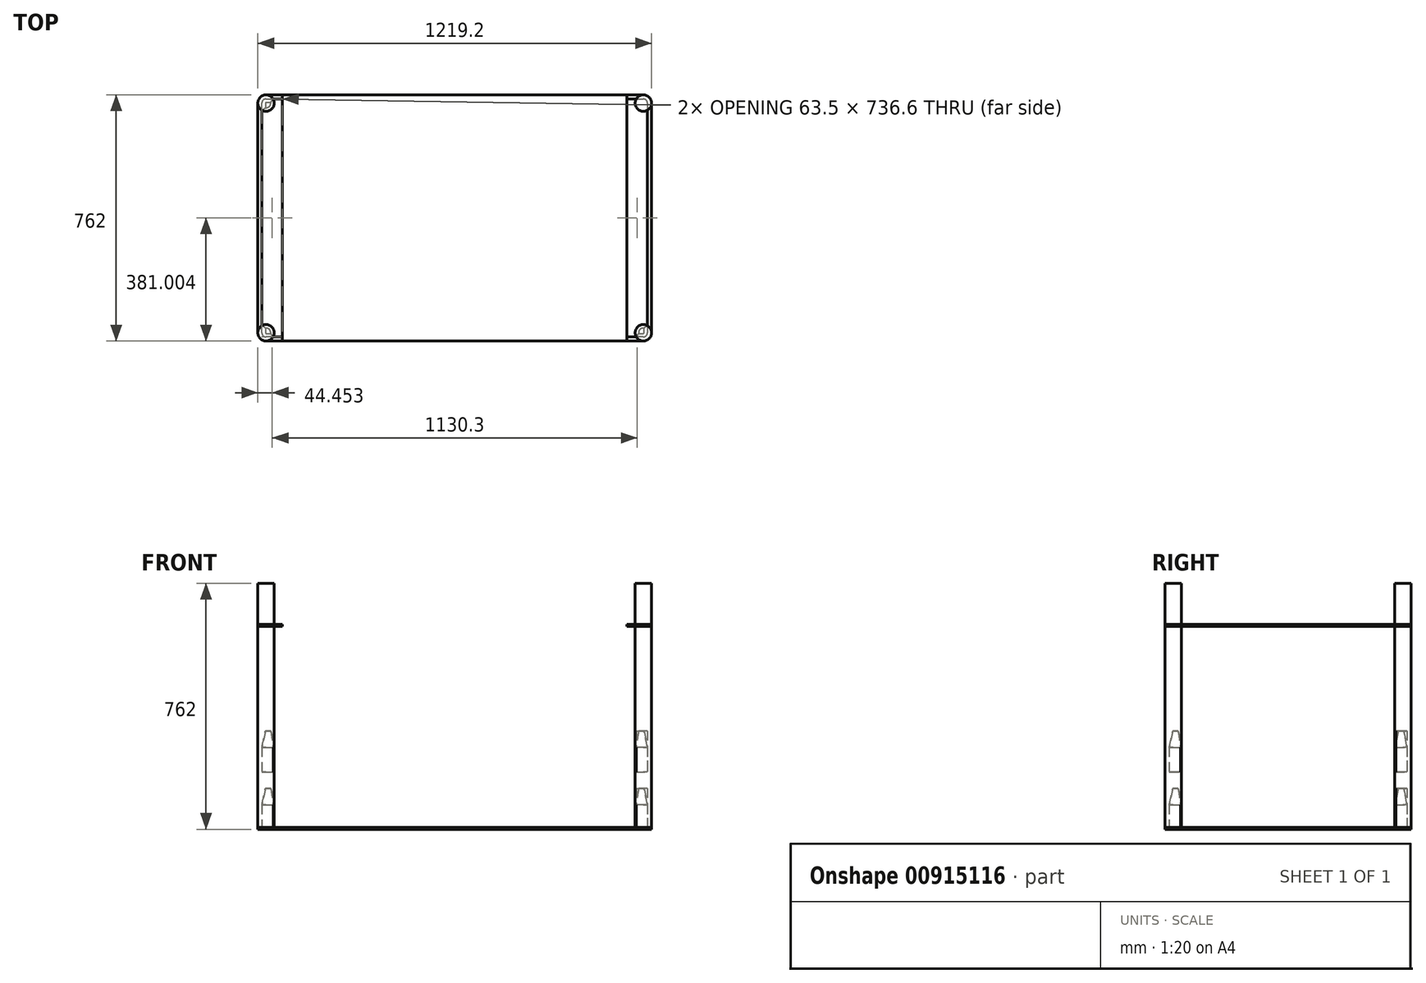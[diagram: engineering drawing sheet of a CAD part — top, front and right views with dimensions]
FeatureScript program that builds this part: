
annotation { "Feature Type Name" : "Feature", "Feature Type Description" : "" }
export const myFeature = defineFeature(function(context is Context, id is Id, definition is map)
    precondition{}
    {
        {
            var Q0;
            Q0=qCreatedBy(makeId("Top.planeOp"),FACE);
            var sketch = newSketch(context, id + "F0", { "sketchPlane" : qUnion([Q0])});
            skLineSegment(sketch, "E0.bottom", {"start": v(-586.7, 384.86) * mm, "end": v(581.7, 384.86) * mm});
            skLineSegment(sketch, "E0.top", {"start": v(-586.7, -377.14) * mm, "end": v(581.7, -377.14) * mm});
            skLineSegment(sketch, "E0.left", {"start": v(-612.1, 359.46) * mm, "end": v(-612.1, -351.74) * mm});
            skLineSegment(sketch, "E0.right", {"start": v(607.1, 359.46) * mm, "end": v(607.1, -351.74) * mm});
            skLineSegment(sketch, "E1", {"start": v(-535.9, 384.86) * mm, "end": v(-535.9, -377.14) * mm});
            skLineSegment(sketch, "E2", {"start": v(530.9, 384.86) * mm, "end": v(530.9, -377.14) * mm});
            skPoint(sketch, "E3.visualSharp", {"position": v(-612.1, 384.86) * mm});
            skArc(sketch, "E3.filletArc", {"start": v(-586.7, 384.86) * mm, "mid": v(-604.67, 377.42) * mm, "end": v(-612.1, 359.46) * mm});
            skPoint(sketch, "E4.visualSharp", {"position": v(-612.1, -377.14) * mm});
            skArc(sketch, "E4.filletArc", {"start": v(-612.1, -351.74) * mm, "mid": v(-604.67, -369.7) * mm, "end": v(-586.7, -377.14) * mm});
            skPoint(sketch, "E5.visualSharp", {"position": v(607.1, 384.86) * mm});
            skArc(sketch, "E5.filletArc", {"start": v(607.1, 359.46) * mm, "mid": v(599.65, 377.42) * mm, "end": v(581.7, 384.86) * mm});
            skPoint(sketch, "E6.visualSharp", {"position": v(607.1, -377.14) * mm});
            skArc(sketch, "E6.filletArc", {"start": v(581.7, -377.14) * mm, "mid": v(599.65, -369.7) * mm, "end": v(607.1, -351.74) * mm});
            skArc(sketch, "E7.0", {"start": v(-586.7, 372.16) * mm, "mid": v(-595.69, 368.44) * mm, "end": v(-599.4, 359.46) * mm});
            skLineSegment(sketch, "E7.1", {"start": v(-586.7, 372.16) * mm, "end": v(581.7, 372.16) * mm});
            skLineSegment(sketch, "E7.2", {"start": v(-599.4, 359.46) * mm, "end": v(-599.4, -351.74) * mm});
            skArc(sketch, "E7.3", {"start": v(594.4, 359.46) * mm, "mid": v(590.67, 368.44) * mm, "end": v(581.7, 372.16) * mm});
            skArc(sketch, "E7.4", {"start": v(-599.4, -351.74) * mm, "mid": v(-595.69, -360.72) * mm, "end": v(-586.7, -364.44) * mm});
            skLineSegment(sketch, "E7.5", {"start": v(-586.7, -364.44) * mm, "end": v(581.7, -364.44) * mm});
            skArc(sketch, "E7.6", {"start": v(581.7, -364.44) * mm, "mid": v(590.67, -360.72) * mm, "end": v(594.4, -351.74) * mm});
            skLineSegment(sketch, "E7.7", {"start": v(594.4, 359.46) * mm, "end": v(594.4, -351.74) * mm});
            skLineSegment(sketch, "E8.right", {"start": v(530.9, 237.71) * mm, "end": v(530.9, -219.49) * mm});
            skLineSegment(sketch, "E9.left", {"start": v(-599.4, 22.91) * mm, "end": v(-599.4, -15.19) * mm});
            skLineSegment(sketch, "E9.right", {"start": v(594.4, 22.91) * mm, "end": v(594.4, -15.19) * mm});
            skLineSegment(sketch, "E10.bottom", {"start": v(-421.6, 372.16) * mm, "end": v(-383.5, 372.16) * mm});
            skLineSegment(sketch, "E10.top", {"start": v(-421.6, -364.44) * mm, "end": v(-383.5, -364.44) * mm});
            skLineSegment(sketch, "E11.bottom", {"start": v(378.5, 372.16) * mm, "end": v(416.6, 372.16) * mm});
            skLineSegment(sketch, "E11.top", {"start": v(378.5, -364.44) * mm, "end": v(416.6, -364.44) * mm});
            skCircle(sketch, "E12", {"center": v(581.7, -351.74) * mm, "radius": 25.4 * mm});
            skCircle(sketch, "E13", {"center": v(581.7, 359.46) * mm, "radius": 25.4 * mm});
            skCircle(sketch, "E14", {"center": v(-586.7, 359.46) * mm, "radius": 25.4 * mm});
            skCircle(sketch, "E15", {"center": v(-586.7, -351.74) * mm, "radius": 25.4 * mm});
            skSolve(sketch);
        }
        {
            var Q0;
            {var subQ0=sQuery(id+"F0.wireOp",EDGE,"RHyDtdP4-Gck5-t29Y-2Plq-2zW18biPkiO3");Q0=makeQuery(id+"F0.imprint","IMPRINT",FACE,{"disambiguationData":[TD([[makeQuery(id+"F0.imprint","IMPRINT",EDGE,{"derivedFrom":subQ0}),1.0]])]});}
            var Q1;
            {var subQ0=sQuery(id+"F0.wireOp",EDGE,"YXO1ubsz-QMrO-05iV-85zx-2RvqL2AsMvx7");Q1=makeQuery(id+"F0.imprint","IMPRINT",FACE,{"disambiguationData":[TD([[makeQuery(id+"F0.imprint","IMPRINT",EDGE,{"derivedFrom":subQ0}),-1.0]])]});}
            var Q2;
            {var subQ0=sQuery(id+"F0.wireOp",EDGE,"1EET5IaC-rPqa-f1PM-2F6D-7rHTKaeenNsA");Q2=makeQuery(id+"F0.imprint","IMPRINT",FACE,{"disambiguationData":[TD([[makeQuery(id+"F0.imprint","IMPRINT",EDGE,{"derivedFrom":subQ0}),-1.0]])]});}
            var Q3;
            {var subQ0=sQuery(id+"F0.wireOp",EDGE,"E8.right");Q3=makeQuery(id+"F0.imprint","IMPRINT",FACE,{"disambiguationData":[TD([[makeQuery(id+"F0.imprint","IMPRINT",EDGE,{"derivedFrom":subQ0}),-1.0]])]});}
            var Q4;
            {var subQ0=sQuery(id+"F0.wireOp",EDGE,"E1");var subQ1=sQuery(id+"F0.wireOp",EDGE,"E0.bottom");var subQ2=makeQuery(id+"F0.imprint","INTERSECT",VERTEX,{"derivedFrom":[subQ1,subQ0]});Q4=makeQuery(id+"F0.imprint","IMPRINT",FACE,{"disambiguationData":[TD([[makeQuery(id+"F0.imprint","IMPRINT",EDGE,{"disambiguationData":[TD([[subQ2,-1.0]])],"derivedFrom":subQ1}),-1.0]])]});}
            var Q5;
            {var subQ0=sQuery(id+"F0.wireOp",EDGE,"E1");var subQ1=sQuery(id+"F0.wireOp",EDGE,"E0.top");var subQ2=makeQuery(id+"F0.imprint","INTERSECT",VERTEX,{"derivedFrom":[subQ1,subQ0]});Q5=makeQuery(id+"F0.imprint","IMPRINT",FACE,{"disambiguationData":[TD([[makeQuery(id+"F0.imprint","IMPRINT",EDGE,{"disambiguationData":[TD([[subQ2,-1.0]])],"derivedFrom":subQ1}),1.0]])]});}
            var Q6;
            Q6=makeQuery(id+"F0.imprint","IMPRINT",FACE,{"disambiguationData":[TD([[makeQuery(id+"F0.imprint","IMPRINT",EDGE,{"derivedFrom":sQuery(id+"F0.wireOp",EDGE,"E0.right")}),-1.0]])]});
            var Q7;
            Q7=makeQuery(id+"F0.imprint","IMPRINT",FACE,{"disambiguationData":[TD([[makeQuery(id+"F0.imprint","IMPRINT",EDGE,{"derivedFrom":sQuery(id+"F0.wireOp",EDGE,"E0.left")}),1.0]])]});
            var Q8;
            {var subQ1=sQuery(id+"F0.wireOp",EDGE,"E7.0");Q8=makeQuery(id+"F0.imprint","IMPRINT",FACE,{"disambiguationData":[TD([[makeQuery(id+"F0.imprint","IMPRINT",EDGE,{"derivedFrom":subQ1}),1.0]])]});}
            var Q9;
            {var subQ0=sQuery(id+"F0.wireOp",EDGE,"E7.3");Q9=makeQuery(id+"F0.imprint","IMPRINT",FACE,{"disambiguationData":[TD([[makeQuery(id+"F0.imprint","IMPRINT",EDGE,{"derivedFrom":subQ0}),1.0]])]});}
            var Q10;
            {var subQ1=sQuery(id+"F0.wireOp",EDGE,"E1");var subQ4=sQuery(id+"F0.wireOp",EDGE,"E7.1");var subQ5=makeQuery(id+"F0.imprint","INTERSECT",VERTEX,{"derivedFrom":[subQ1,subQ4]});Q10=makeQuery(id+"F0.imprint","IMPRINT",FACE,{"disambiguationData":[TD([[makeQuery(id+"F0.imprint","IMPRINT",EDGE,{"disambiguationData":[TD([[subQ5,-1.0]])],"derivedFrom":subQ4}),-1.0]])]});}
            var Q11;
            {var subQ1=sQuery(id+"F0.wireOp",EDGE,"E1");var subQ4=sQuery(id+"F0.wireOp",EDGE,"E7.5");var subQ5=makeQuery(id+"F0.imprint","INTERSECT",VERTEX,{"derivedFrom":[subQ1,subQ4]});Q11=makeQuery(id+"F0.imprint","IMPRINT",FACE,{"disambiguationData":[TD([[makeQuery(id+"F0.imprint","IMPRINT",EDGE,{"disambiguationData":[TD([[subQ5,-1.0]])],"derivedFrom":subQ4}),1.0]])]});}
            var Q12;
            {var subQ0=sQuery(id+"F0.wireOp",EDGE,"E8.left");Q12=makeQuery(id+"F0.imprint","IMPRINT",FACE,{"disambiguationData":[TD([[makeQuery(id+"F0.imprint","IMPRINT",EDGE,{"derivedFrom":subQ0}),1.0]])]});}
            var Q13;
            {var subQ0=sQuery(id+"F0.wireOp",EDGE,"E7.4");Q13=makeQuery(id+"F0.imprint","IMPRINT",FACE,{"disambiguationData":[TD([[makeQuery(id+"F0.imprint","IMPRINT",EDGE,{"derivedFrom":subQ0}),1.0]])]});}
            var Q14;
            {var subQ5=sQuery(id+"F0.wireOp",EDGE,"E9.left");Q14=makeQuery(id+"F0.imprint","IMPRINT",FACE,{"disambiguationData":[TD([[makeQuery(id+"F0.imprint","IMPRINT",EDGE,{"derivedFrom":subQ5}),1.0]])]});}
            var Q15;
            {var subQ0=sQuery(id+"F0.wireOp",EDGE,"E9.bottom");var subQ1=sQuery(id+"F0.wireOp",EDGE,"E1");var subQ2=makeQuery(id+"F0.imprint","INTERSECT",VERTEX,{"derivedFrom":[subQ1,subQ0]});Q15=makeQuery(id+"F0.imprint","IMPRINT",FACE,{"disambiguationData":[TD([[makeQuery(id+"F0.imprint","IMPRINT",EDGE,{"disambiguationData":[TD([[subQ2,-1.0]])],"derivedFrom":subQ1}),1.0]])]});}
            var Q16;
            {var subQ0=sQuery(id+"F0.wireOp",EDGE,"E10.right");var subQ5=sQuery(id+"F0.wireOp",EDGE,"E9.top");var subQ6=makeQuery(id+"F0.imprint","INTERSECT",VERTEX,{"derivedFrom":[subQ5,subQ0]});Q16=makeQuery(id+"F0.imprint","IMPRINT",FACE,{"disambiguationData":[TD([[makeQuery(id+"F0.imprint","IMPRINT",EDGE,{"disambiguationData":[TD([[subQ6,-1.0]])],"derivedFrom":subQ5}),-1.0]])]});}
            var Q17;
            {var subQ0=sQuery(id+"F0.wireOp",EDGE,"E10.right");var subQ5=sQuery(id+"F0.wireOp",EDGE,"E9.bottom");var subQ6=makeQuery(id+"F0.imprint","INTERSECT",VERTEX,{"derivedFrom":[subQ5,subQ0]});Q17=makeQuery(id+"F0.imprint","IMPRINT",FACE,{"disambiguationData":[TD([[makeQuery(id+"F0.imprint","IMPRINT",EDGE,{"disambiguationData":[TD([[subQ6,-1.0]])],"derivedFrom":subQ5}),1.0]])]});}
            var Q18;
            {var subQ5=sQuery(id+"F0.wireOp",EDGE,"E10.bottom");Q18=makeQuery(id+"F0.imprint","IMPRINT",FACE,{"disambiguationData":[TD([[makeQuery(id+"F0.imprint","IMPRINT",EDGE,{"derivedFrom":subQ5}),-1.0]])]});}
            var Q19;
            {var subQ0=sQuery(id+"F0.wireOp",EDGE,"E10.left");var subQ1=sQuery(id+"F0.wireOp",EDGE,"E9.bottom");var subQ2=makeQuery(id+"F0.imprint","INTERSECT",VERTEX,{"derivedFrom":[subQ1,subQ0]});Q19=makeQuery(id+"F0.imprint","IMPRINT",FACE,{"disambiguationData":[TD([[makeQuery(id+"F0.imprint","IMPRINT",EDGE,{"disambiguationData":[TD([[subQ2,-1.0]])],"derivedFrom":subQ1}),-1.0]])]});}
            var Q20;
            {var subQ5=sQuery(id+"F0.wireOp",EDGE,"E10.top");Q20=makeQuery(id+"F0.imprint","IMPRINT",FACE,{"disambiguationData":[TD([[makeQuery(id+"F0.imprint","IMPRINT",EDGE,{"derivedFrom":subQ5}),1.0]])]});}
            var Q21;
            {var subQ0=sQuery(id+"F0.wireOp",EDGE,"E10.right");var subQ1=sQuery(id+"F0.wireOp",EDGE,"E9.bottom");var subQ2=makeQuery(id+"F0.imprint","INTERSECT",VERTEX,{"derivedFrom":[subQ1,subQ0]});Q21=makeQuery(id+"F0.imprint","IMPRINT",FACE,{"disambiguationData":[TD([[makeQuery(id+"F0.imprint","IMPRINT",EDGE,{"disambiguationData":[TD([[subQ2,-1.0]])],"derivedFrom":subQ1}),-1.0]])]});}
            var Q22;
            {var subQ0=sQuery(id+"F0.wireOp",EDGE,"E8.right");var subQ1=sQuery(id+"F0.wireOp",EDGE,"E2");var subQ2=makeQuery(id+"F0.imprint","INTERSECT",VERTEX,{"disambiguationData":[OD(1.0)],"derivedFrom":[subQ1,subQ0]});Q22=makeQuery(id+"F0.imprint","IMPRINT",FACE,{"disambiguationData":[TD([[makeQuery(id+"F0.imprint","IMPRINT",EDGE,{"disambiguationData":[TD([[subQ2,-1.0]])],"derivedFrom":subQ1}),-1.0]])]});}
            var Q23;
            {var subQ1=sQuery(id+"F0.wireOp",EDGE,"E8.right");var subQ7=sQuery(id+"F0.wireOp",EDGE,"E2");var subQ9=makeQuery(id+"F0.imprint","INTERSECT",VERTEX,{"disambiguationData":[OD(0.0)],"derivedFrom":[subQ7,subQ1]});Q23=makeQuery(id+"F0.imprint","IMPRINT",FACE,{"disambiguationData":[TD([[makeQuery(id+"F0.imprint","IMPRINT",EDGE,{"disambiguationData":[TD([[subQ9,1.0]])],"derivedFrom":subQ7}),-1.0]])]});}
            var Q24;
            {var subQ5=sQuery(id+"F0.wireOp",EDGE,"E11.bottom");Q24=makeQuery(id+"F0.imprint","IMPRINT",FACE,{"disambiguationData":[TD([[makeQuery(id+"F0.imprint","IMPRINT",EDGE,{"derivedFrom":subQ5}),-1.0]])]});}
            var Q25;
            {var subQ0=sQuery(id+"F0.wireOp",EDGE,"E11.left");var subQ1=sQuery(id+"F0.wireOp",EDGE,"E9.bottom");var subQ2=makeQuery(id+"F0.imprint","INTERSECT",VERTEX,{"derivedFrom":[subQ1,subQ0]});Q25=makeQuery(id+"F0.imprint","IMPRINT",FACE,{"disambiguationData":[TD([[makeQuery(id+"F0.imprint","IMPRINT",EDGE,{"disambiguationData":[TD([[subQ2,-1.0]])],"derivedFrom":subQ1}),-1.0]])]});}
            var Q26;
            {var subQ5=sQuery(id+"F0.wireOp",EDGE,"E11.top");Q26=makeQuery(id+"F0.imprint","IMPRINT",FACE,{"disambiguationData":[TD([[makeQuery(id+"F0.imprint","IMPRINT",EDGE,{"derivedFrom":subQ5}),1.0]])]});}
            var Q27;
            {var subQ1=sQuery(id+"F0.wireOp",EDGE,"E7.6");Q27=makeQuery(id+"F0.imprint","IMPRINT",FACE,{"disambiguationData":[TD([[makeQuery(id+"F0.imprint","IMPRINT",EDGE,{"derivedFrom":subQ1}),1.0]])]});}
            var Q28;
            {var subQ5=sQuery(id+"F0.wireOp",EDGE,"E9.right");Q28=makeQuery(id+"F0.imprint","IMPRINT",FACE,{"disambiguationData":[TD([[makeQuery(id+"F0.imprint","IMPRINT",EDGE,{"derivedFrom":subQ5}),-1.0]])]});}
            var Q29;
            {var subQ4=sQuery(id+"F0.wireOp",EDGE,"E7.6");Q29=makeQuery(id+"F0.imprint","IMPRINT",FACE,{"disambiguationData":[TD([[makeQuery(id+"F0.imprint","IMPRINT",EDGE,{"derivedFrom":subQ4}),-1.0]])]});}
            var Q30;
            {var subQ0=sQuery(id+"F0.wireOp",EDGE,"E12");var subQ1=sQuery(id+"F0.wireOp",EDGE,"E0.top");var subQ2=makeQuery(id+"F0.imprint","INTERSECT",VERTEX,{"derivedFrom":[subQ1,subQ0]});Q30=makeQuery(id+"F0.imprint","IMPRINT",FACE,{"disambiguationData":[TD([[makeQuery(id+"F0.imprint","IMPRINT",EDGE,{"disambiguationData":[TD([[subQ2,1.0]])],"derivedFrom":subQ1}),1.0]])]});}
            var Q31;
            {var subQ4=sQuery(id+"F0.wireOp",EDGE,"E7.3");Q31=makeQuery(id+"F0.imprint","IMPRINT",FACE,{"disambiguationData":[TD([[makeQuery(id+"F0.imprint","IMPRINT",EDGE,{"derivedFrom":subQ4}),-1.0]])]});}
            var Q32;
            {var subQ0=sQuery(id+"F0.wireOp",EDGE,"E13");var subQ1=sQuery(id+"F0.wireOp",EDGE,"E0.bottom");var subQ2=makeQuery(id+"F0.imprint","INTERSECT",VERTEX,{"derivedFrom":[subQ1,subQ0]});Q32=makeQuery(id+"F0.imprint","IMPRINT",FACE,{"disambiguationData":[TD([[makeQuery(id+"F0.imprint","IMPRINT",EDGE,{"disambiguationData":[TD([[subQ2,1.0]])],"derivedFrom":subQ1}),-1.0]])]});}
            var Q33;
            {var subQ0=sQuery(id+"F0.wireOp",EDGE,"E15");var subQ1=sQuery(id+"F0.wireOp",EDGE,"E0.top");var subQ2=makeQuery(id+"F0.imprint","INTERSECT",VERTEX,{"derivedFrom":[subQ1,subQ0]});Q33=makeQuery(id+"F0.imprint","IMPRINT",FACE,{"disambiguationData":[TD([[makeQuery(id+"F0.imprint","IMPRINT",EDGE,{"disambiguationData":[TD([[subQ2,-1.0]])],"derivedFrom":subQ1}),1.0]])]});}
            var Q34;
            {var subQ5=sQuery(id+"F0.wireOp",EDGE,"E7.4");Q34=makeQuery(id+"F0.imprint","IMPRINT",FACE,{"disambiguationData":[TD([[makeQuery(id+"F0.imprint","IMPRINT",EDGE,{"derivedFrom":subQ5}),-1.0]])]});}
            var Q35;
            {var subQ0=sQuery(id+"F0.wireOp",EDGE,"E14");var subQ1=sQuery(id+"F0.wireOp",EDGE,"E0.bottom");var subQ2=makeQuery(id+"F0.imprint","INTERSECT",VERTEX,{"derivedFrom":[subQ1,subQ0]});Q35=makeQuery(id+"F0.imprint","IMPRINT",FACE,{"disambiguationData":[TD([[makeQuery(id+"F0.imprint","IMPRINT",EDGE,{"disambiguationData":[TD([[subQ2,-1.0]])],"derivedFrom":subQ1}),-1.0]])]});}
            var Q36;
            {var subQ1=sQuery(id+"F0.wireOp",EDGE,"E7.0");Q36=makeQuery(id+"F0.imprint","IMPRINT",FACE,{"disambiguationData":[TD([[makeQuery(id+"F0.imprint","IMPRINT",EDGE,{"derivedFrom":subQ1}),-1.0]])]});}
            extrude(context, id + "F1", {"entities" : qUnion([Q0, Q1, Q2, Q3, Q4, Q5, Q6, Q7, Q8, Q9, Q10, Q11, Q12, Q13, Q14, Q15, Q16, Q17, Q18, Q19, Q20, Q21, Q22, Q23, Q24, Q25, Q26, Q27, Q28, Q29, Q30, Q31, Q32, Q33, Q34, Q35, Q36]), "depth" : 6.35 * mm, "offsetDistance" : 25.4 * mm});
        }
        {
            var Q0;
            {var subQ9=sQuery(id+"F0.wireOp",EDGE,"E8.right");Q0=makeQuery(id+"F0.imprint","IMPRINT",FACE,{"disambiguationData":[TD([[makeQuery(id+"F0.imprint","IMPRINT",EDGE,{"derivedFrom":subQ9}),-1.0]])]});}
            var Q1;
            {var subQ0=sQuery(id+"F0.wireOp",EDGE,"E9.left");Q1=makeQuery(id+"F0.imprint","IMPRINT",FACE,{"disambiguationData":[TD([[makeQuery(id+"F0.imprint","IMPRINT",EDGE,{"derivedFrom":subQ0}),1.0]])]});}
            var Q2;
            {var subQ5=sQuery(id+"F0.wireOp",EDGE,"E8.right");Q2=makeQuery(id+"F0.imprint","IMPRINT",FACE,{"disambiguationData":[TD([[makeQuery(id+"F0.imprint","IMPRINT",EDGE,{"derivedFrom":subQ5}),1.0]])]});}
            var Q3;
            {var subQ0=sQuery(id+"F0.wireOp",EDGE,"E7.0");Q3=makeQuery(id+"F0.imprint","IMPRINT",FACE,{"disambiguationData":[TD([[makeQuery(id+"F0.imprint","IMPRINT",EDGE,{"derivedFrom":subQ0}),1.0]])]});}
            var Q4;
            {var subQ0=sQuery(id+"F0.wireOp",EDGE,"E7.3");Q4=makeQuery(id+"F0.imprint","IMPRINT",FACE,{"disambiguationData":[TD([[makeQuery(id+"F0.imprint","IMPRINT",EDGE,{"derivedFrom":subQ0}),1.0]])]});}
            var Q5;
            {var subQ0=sQuery(id+"F0.wireOp",EDGE,"E7.4");Q5=makeQuery(id+"F0.imprint","IMPRINT",FACE,{"disambiguationData":[TD([[makeQuery(id+"F0.imprint","IMPRINT",EDGE,{"derivedFrom":subQ0}),1.0]])]});}
            var Q6;
            {var subQ0=sQuery(id+"F0.wireOp",EDGE,"E7.6");Q6=makeQuery(id+"F0.imprint","IMPRINT",FACE,{"disambiguationData":[TD([[makeQuery(id+"F0.imprint","IMPRINT",EDGE,{"derivedFrom":subQ0}),1.0]])]});}
            extrude(context, id + "F2", {"entities" : qUnion([Q0, Q1, Q2, Q3, Q4, Q5, Q6]), "depth" : 127 * mm, "offsetDistance" : 25.4 * mm, "hasSecondDirection" : true, "secondDirectionOppositeDirection" : false, "secondDirectionDepth" : 6.35 * mm});
        }
        {
            var Q0;
            Q0=makeQuery(id+"F2.opExtrude","CAP_FACE",FACE,{"disambiguationData":[OSD([sQuery(id+"F0.wireOp",EDGE,"E7.0"),sQuery(id+"F0.wireOp",EDGE,"E7.1"),sQuery(id+"F0.wireOp",EDGE,"E7.2"),sQuery(id+"F0.wireOp",EDGE,"E7.3"),sQuery(id+"F0.wireOp",EDGE,"E7.4"),sQuery(id+"F0.wireOp",EDGE,"E7.5"),sQuery(id+"F0.wireOp",EDGE,"E7.6"),sQuery(id+"F0.wireOp",EDGE,"E7.7"),sQuery(id+"F0.wireOp",EDGE,"E9.left"),sQuery(id+"F0.wireOp",EDGE,"E9.right"),sQuery(id+"F0.wireOp",EDGE,"E10.bottom"),sQuery(id+"F0.wireOp",EDGE,"E10.top"),sQuery(id+"F0.wireOp",EDGE,"E11.bottom"),sQuery(id+"F0.wireOp",EDGE,"E11.top")])],"isStart":false});
            chamfer(context, id + "F3", {"entities" : qUnion([Q0]), "chamferType" : ChamferType.OFFSET_ANGLE, "width" : 50.8 * mm, "oppositeDirection" : true, "angle" : 12 * degree, "tangentPropagation" : true});
        }
        {
            var Q0;
            {var subQ4=sQuery(id+"F0.wireOp",EDGE,"E7.6");Q0=makeQuery(id+"F0.imprint","IMPRINT",FACE,{"disambiguationData":[TD([[makeQuery(id+"F0.imprint","IMPRINT",EDGE,{"derivedFrom":subQ4}),-1.0]])]});}
            var Q1;
            {var subQ0=sQuery(id+"F0.wireOp",EDGE,"E7.6");Q1=makeQuery(id+"F0.imprint","IMPRINT",FACE,{"disambiguationData":[TD([[makeQuery(id+"F0.imprint","IMPRINT",EDGE,{"derivedFrom":subQ0}),1.0]])]});}
            var Q2;
            {var subQ0=sQuery(id+"F0.wireOp",EDGE,"E7.0");Q2=makeQuery(id+"F0.imprint","IMPRINT",FACE,{"disambiguationData":[TD([[makeQuery(id+"F0.imprint","IMPRINT",EDGE,{"derivedFrom":subQ0}),1.0]])]});}
            var Q3;
            {var subQ1=sQuery(id+"F0.wireOp",EDGE,"E7.0");Q3=makeQuery(id+"F0.imprint","IMPRINT",FACE,{"disambiguationData":[TD([[makeQuery(id+"F0.imprint","IMPRINT",EDGE,{"derivedFrom":subQ1}),-1.0]])]});}
            var Q4;
            {var subQ0=sQuery(id+"F0.wireOp",EDGE,"E7.4");Q4=makeQuery(id+"F0.imprint","IMPRINT",FACE,{"disambiguationData":[TD([[makeQuery(id+"F0.imprint","IMPRINT",EDGE,{"derivedFrom":subQ0}),1.0]])]});}
            var Q5;
            {var subQ5=sQuery(id+"F0.wireOp",EDGE,"E7.4");Q5=makeQuery(id+"F0.imprint","IMPRINT",FACE,{"disambiguationData":[TD([[makeQuery(id+"F0.imprint","IMPRINT",EDGE,{"derivedFrom":subQ5}),-1.0]])]});}
            var Q6;
            {var subQ4=sQuery(id+"F0.wireOp",EDGE,"E7.3");Q6=makeQuery(id+"F0.imprint","IMPRINT",FACE,{"disambiguationData":[TD([[makeQuery(id+"F0.imprint","IMPRINT",EDGE,{"derivedFrom":subQ4}),-1.0]])]});}
            var Q7;
            {var subQ0=sQuery(id+"F0.wireOp",EDGE,"E7.3");Q7=makeQuery(id+"F0.imprint","IMPRINT",FACE,{"disambiguationData":[TD([[makeQuery(id+"F0.imprint","IMPRINT",EDGE,{"derivedFrom":subQ0}),1.0]])]});}
            extrude(context, id + "F4", {"entities" : qUnion([Q0, Q1, Q2, Q3, Q4, Q5, Q6, Q7]), "depth" : 762 * mm, "offsetDistance" : 25.4 * mm, "hasSecondDirection" : true, "secondDirectionOppositeDirection" : false, "secondDirectionDepth" : 6.35 * mm});
        }
        {
            var Q0;
            {var subQ5=sQuery(id+"F0.wireOp",EDGE,"E0.left");Q0=makeQuery(id+"F0.imprint","IMPRINT",FACE,{"disambiguationData":[TD([[makeQuery(id+"F0.imprint","IMPRINT",EDGE,{"derivedFrom":subQ5}),1.0]])]});}
            var Q1;
            {var subQ0=sQuery(id+"F0.wireOp",EDGE,"E9.left");Q1=makeQuery(id+"F0.imprint","IMPRINT",FACE,{"disambiguationData":[TD([[makeQuery(id+"F0.imprint","IMPRINT",EDGE,{"derivedFrom":subQ0}),1.0]])]});}
            var Q2;
            {var subQ0=sQuery(id+"F0.wireOp",EDGE,"E7.0");Q2=makeQuery(id+"F0.imprint","IMPRINT",FACE,{"disambiguationData":[TD([[makeQuery(id+"F0.imprint","IMPRINT",EDGE,{"derivedFrom":subQ0}),1.0]])]});}
            var Q3;
            {var subQ1=sQuery(id+"F0.wireOp",EDGE,"E7.0");Q3=makeQuery(id+"F0.imprint","IMPRINT",FACE,{"disambiguationData":[TD([[makeQuery(id+"F0.imprint","IMPRINT",EDGE,{"derivedFrom":subQ1}),-1.0]])]});}
            var Q4;
            {var subQ9=sQuery(id+"F0.wireOp",EDGE,"E8.right");Q4=makeQuery(id+"F0.imprint","IMPRINT",FACE,{"disambiguationData":[TD([[makeQuery(id+"F0.imprint","IMPRINT",EDGE,{"derivedFrom":subQ9}),-1.0]])]});}
            var Q5;
            {var subQ0=sQuery(id+"F0.wireOp",EDGE,"E14");var subQ1=sQuery(id+"F0.wireOp",EDGE,"E0.bottom");var subQ2=makeQuery(id+"F0.imprint","INTERSECT",VERTEX,{"derivedFrom":[subQ1,subQ0]});Q5=makeQuery(id+"F0.imprint","IMPRINT",FACE,{"disambiguationData":[TD([[makeQuery(id+"F0.imprint","IMPRINT",EDGE,{"disambiguationData":[TD([[subQ2,-1.0]])],"derivedFrom":subQ1}),-1.0]])]});}
            var Q6;
            {var subQ0=sQuery(id+"F0.wireOp",EDGE,"E10.bottom");Q6=makeQuery(id+"F0.imprint","IMPRINT",FACE,{"disambiguationData":[TD([[makeQuery(id+"F0.imprint","IMPRINT",EDGE,{"derivedFrom":subQ0}),1.0]])]});}
            var Q7;
            {var subQ5=sQuery(id+"F0.wireOp",EDGE,"E7.4");Q7=makeQuery(id+"F0.imprint","IMPRINT",FACE,{"disambiguationData":[TD([[makeQuery(id+"F0.imprint","IMPRINT",EDGE,{"derivedFrom":subQ5}),-1.0]])]});}
            var Q8;
            {var subQ0=sQuery(id+"F0.wireOp",EDGE,"E7.4");Q8=makeQuery(id+"F0.imprint","IMPRINT",FACE,{"disambiguationData":[TD([[makeQuery(id+"F0.imprint","IMPRINT",EDGE,{"derivedFrom":subQ0}),1.0]])]});}
            var Q9;
            {var subQ0=sQuery(id+"F0.wireOp",EDGE,"E15");var subQ1=sQuery(id+"F0.wireOp",EDGE,"E0.top");var subQ2=makeQuery(id+"F0.imprint","INTERSECT",VERTEX,{"derivedFrom":[subQ1,subQ0]});Q9=makeQuery(id+"F0.imprint","IMPRINT",FACE,{"disambiguationData":[TD([[makeQuery(id+"F0.imprint","IMPRINT",EDGE,{"disambiguationData":[TD([[subQ2,-1.0]])],"derivedFrom":subQ1}),1.0]])]});}
            var Q10;
            {var subQ0=sQuery(id+"F0.wireOp",EDGE,"E10.top");Q10=makeQuery(id+"F0.imprint","IMPRINT",FACE,{"disambiguationData":[TD([[makeQuery(id+"F0.imprint","IMPRINT",EDGE,{"derivedFrom":subQ0}),-1.0]])]});}
            var Q11;
            {var subQ0=sQuery(id+"F0.wireOp",EDGE,"E13");var subQ1=sQuery(id+"F0.wireOp",EDGE,"E0.bottom");var subQ2=makeQuery(id+"F0.imprint","INTERSECT",VERTEX,{"derivedFrom":[subQ1,subQ0]});Q11=makeQuery(id+"F0.imprint","IMPRINT",FACE,{"disambiguationData":[TD([[makeQuery(id+"F0.imprint","IMPRINT",EDGE,{"disambiguationData":[TD([[subQ2,1.0]])],"derivedFrom":subQ1}),-1.0]])]});}
            var Q12;
            {var subQ0=sQuery(id+"F0.wireOp",EDGE,"E7.3");Q12=makeQuery(id+"F0.imprint","IMPRINT",FACE,{"disambiguationData":[TD([[makeQuery(id+"F0.imprint","IMPRINT",EDGE,{"derivedFrom":subQ0}),1.0]])]});}
            var Q13;
            {var subQ5=sQuery(id+"F0.wireOp",EDGE,"E8.right");Q13=makeQuery(id+"F0.imprint","IMPRINT",FACE,{"disambiguationData":[TD([[makeQuery(id+"F0.imprint","IMPRINT",EDGE,{"derivedFrom":subQ5}),1.0]])]});}
            var Q14;
            {var subQ6=sQuery(id+"F0.wireOp",EDGE,"E0.right");Q14=makeQuery(id+"F0.imprint","IMPRINT",FACE,{"disambiguationData":[TD([[makeQuery(id+"F0.imprint","IMPRINT",EDGE,{"derivedFrom":subQ6}),-1.0]])]});}
            var Q15;
            {var subQ4=sQuery(id+"F0.wireOp",EDGE,"E7.3");Q15=makeQuery(id+"F0.imprint","IMPRINT",FACE,{"disambiguationData":[TD([[makeQuery(id+"F0.imprint","IMPRINT",EDGE,{"derivedFrom":subQ4}),-1.0]])]});}
            var Q16;
            {var subQ0=sQuery(id+"F0.wireOp",EDGE,"E12");var subQ1=sQuery(id+"F0.wireOp",EDGE,"E0.top");var subQ2=makeQuery(id+"F0.imprint","INTERSECT",VERTEX,{"derivedFrom":[subQ1,subQ0]});Q16=makeQuery(id+"F0.imprint","IMPRINT",FACE,{"disambiguationData":[TD([[makeQuery(id+"F0.imprint","IMPRINT",EDGE,{"disambiguationData":[TD([[subQ2,1.0]])],"derivedFrom":subQ1}),1.0]])]});}
            var Q17;
            {var subQ0=sQuery(id+"F0.wireOp",EDGE,"E7.6");Q17=makeQuery(id+"F0.imprint","IMPRINT",FACE,{"disambiguationData":[TD([[makeQuery(id+"F0.imprint","IMPRINT",EDGE,{"derivedFrom":subQ0}),1.0]])]});}
            var Q18;
            {var subQ4=sQuery(id+"F0.wireOp",EDGE,"E7.6");Q18=makeQuery(id+"F0.imprint","IMPRINT",FACE,{"disambiguationData":[TD([[makeQuery(id+"F0.imprint","IMPRINT",EDGE,{"derivedFrom":subQ4}),-1.0]])]});}
            extrude(context, id + "F5", {"entities" : qUnion([Q0, Q1, Q2, Q3, Q4, Q5, Q6, Q7, Q8, Q9, Q10, Q11, Q12, Q13, Q14, Q15, Q16, Q17, Q18]), "depth" : 635 * mm, "offsetDistance" : 25.4 * mm, "hasSecondDirection" : true, "secondDirectionOppositeDirection" : false, "secondDirectionDepth" : 628.65 * mm});
        }
        {
            var Q0;
            {var subQ0=sQuery(id+"F0.wireOp",EDGE,"E7.0");Q0=makeQuery(id+"F0.imprint","IMPRINT",FACE,{"disambiguationData":[TD([[makeQuery(id+"F0.imprint","IMPRINT",EDGE,{"derivedFrom":subQ0}),1.0]])]});}
            var Q1;
            {var subQ0=sQuery(id+"F0.wireOp",EDGE,"E9.left");Q1=makeQuery(id+"F0.imprint","IMPRINT",FACE,{"disambiguationData":[TD([[makeQuery(id+"F0.imprint","IMPRINT",EDGE,{"derivedFrom":subQ0}),1.0]])]});}
            var Q2;
            {var subQ9=sQuery(id+"F0.wireOp",EDGE,"E8.right");Q2=makeQuery(id+"F0.imprint","IMPRINT",FACE,{"disambiguationData":[TD([[makeQuery(id+"F0.imprint","IMPRINT",EDGE,{"derivedFrom":subQ9}),-1.0]])]});}
            var Q3;
            {var subQ0=sQuery(id+"F0.wireOp",EDGE,"E7.4");Q3=makeQuery(id+"F0.imprint","IMPRINT",FACE,{"disambiguationData":[TD([[makeQuery(id+"F0.imprint","IMPRINT",EDGE,{"derivedFrom":subQ0}),1.0]])]});}
            var Q4;
            {var subQ0=sQuery(id+"F0.wireOp",EDGE,"E7.3");Q4=makeQuery(id+"F0.imprint","IMPRINT",FACE,{"disambiguationData":[TD([[makeQuery(id+"F0.imprint","IMPRINT",EDGE,{"derivedFrom":subQ0}),1.0]])]});}
            var Q5;
            {var subQ5=sQuery(id+"F0.wireOp",EDGE,"E8.right");Q5=makeQuery(id+"F0.imprint","IMPRINT",FACE,{"disambiguationData":[TD([[makeQuery(id+"F0.imprint","IMPRINT",EDGE,{"derivedFrom":subQ5}),1.0]])]});}
            var Q6;
            {var subQ0=sQuery(id+"F0.wireOp",EDGE,"E7.6");Q6=makeQuery(id+"F0.imprint","IMPRINT",FACE,{"disambiguationData":[TD([[makeQuery(id+"F0.imprint","IMPRINT",EDGE,{"derivedFrom":subQ0}),1.0]])]});}
            extrude(context, id + "F6", {"entities" : qUnion([Q0, Q1, Q2, Q3, Q4, Q5, Q6]), "depth" : 304.8 * mm, "offsetDistance" : 25.4 * mm, "hasSecondDirection" : true, "secondDirectionOppositeDirection" : false, "secondDirectionDepth" : 177.8 * mm});
        }
        {
            var Q0;
            Q0=makeQuery(id+"F6.opExtrude","CAP_FACE",FACE,{"disambiguationData":[OSD([sQuery(id+"F0.wireOp",EDGE,"E7.0"),sQuery(id+"F0.wireOp",EDGE,"E7.1"),sQuery(id+"F0.wireOp",EDGE,"E7.2"),sQuery(id+"F0.wireOp",EDGE,"E7.3"),sQuery(id+"F0.wireOp",EDGE,"E7.4"),sQuery(id+"F0.wireOp",EDGE,"E7.5"),sQuery(id+"F0.wireOp",EDGE,"E7.6"),sQuery(id+"F0.wireOp",EDGE,"E7.7"),sQuery(id+"F0.wireOp",EDGE,"E9.left"),sQuery(id+"F0.wireOp",EDGE,"E9.right"),sQuery(id+"F0.wireOp",EDGE,"E10.bottom"),sQuery(id+"F0.wireOp",EDGE,"E10.top"),sQuery(id+"F0.wireOp",EDGE,"E11.bottom"),sQuery(id+"F0.wireOp",EDGE,"E11.top")])],"isStart":false});
            chamfer(context, id + "F7", {"entities" : qUnion([Q0]), "chamferType" : ChamferType.OFFSET_ANGLE, "width" : 50.8 * mm, "oppositeDirection" : true, "angle" : 12 * degree, "tangentPropagation" : true});
        }
    });
